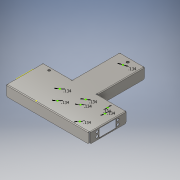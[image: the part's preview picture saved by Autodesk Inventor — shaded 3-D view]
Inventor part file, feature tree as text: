
AUTODESK INVENTOR PART (.ipt)
format: ipt  version: 2016 (Build 200138000, 138)  size: 503,808 bytes
history: native  units: in
note: dims shown in document units (in); Inventor stores cm internally (conversion verified against a paired STEP export)
features: other x15, sketch x13, sheet_metal_op x6, fillet x3
ambient origin geometry x8: Origin, YZ Plane, XZ Plane, XY Plane, X Axis, Y Axis, Z Axis, Center Point
bodies: Solid1 (feature_tree)
feature tree (37):
  sheet_metal_op  "Face1"
  sheet_metal_op  "Face2"
  sheet_metal_op  "Flange1"
  sketch  "Sketch9"  dims[d12=3.4374in]
  sketch  "Sketch18"  dims[d14=0.034in]
  sketch  "Sketch21"  dims[d16=0.068in]
  sketch  "Sketch22"  dims[d17=0.034in]
  fillet  "Fillet1"  Radius=2.3in
  fillet  "Fillet2"  Radius=8.0in
  fillet  "Fillet3"  Radius=0.034in
  sketch  "Sketch24"  dims[d19=0.017in]
  sketch  "Sketch25"  dims[d20=0.068in]
  sketch  "Sketch26"  dims[d21=0.034in d22=1.0in d23=90.0deg d24=0.034in d25=0.136in d26=0.034in d27=0.034in d40=0.034in d41=0.0in d42=0.8in d53=0.917in d55=0.034in d56=0.0in d57=0.917in d64=45.0deg d65=0.034in d66=0.0in d67=0.917in d71=1.625in d72=12.0in d73=0.0in d74=12.0in d75=0.0in d76=0.034in d77=0.0in d78=0.034in d79=0.0in d81=0.034in d82=0.0in d83=0.125in d84=0.125in d85=0.125in d86=0.231in d87=0.25in d92=0.134in d93=0.134in d94=0.134in d96=0.134in d99=0.134in d100=0.134in d101=0.134in d102=0.134in d103=0.034in d104=0.0in d105=0.034in d106=0.0in d107=0.034in d108=0.0in]
  sketch  "Sketch2"  dims[d9=3.4374in]
  other  "Plate1"
  sketch  "Sketch4"  dims[d10=2.7993in]
  other  "Plate2"
  sheet_metal_op  "Bend1"
  sketch  "Sketch5"  dims[d11=2.799in]
  other  "Plate3"
  sheet_metal_op  "Bend2"
  sheet_metal_op  "Corner1"
  sketch  "Sketch13"  dims[d13=0.034in]
  sketch  "Sketch20"  dims[d15=0.017in]
  sketch  "Sketch23"  dims[d18=0.034in]
  other  "Cut5"
  other  "Cut7"
  other  "Cut10"
  other  "Cut12"
  other  "Cut13"
  other  "Cut14"
  other  "Cut15"
  other  "Cut16"
  other  "Cut17"
  other  "Cut18"
  other  "Cut19"
  other  "Definition1"
